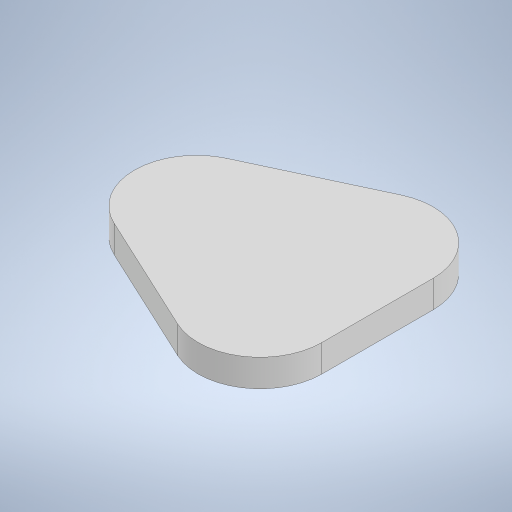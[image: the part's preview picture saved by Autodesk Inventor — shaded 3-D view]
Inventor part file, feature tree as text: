
AUTODESK INVENTOR PART (.ipt)
format: ipt  version: 2024.3 (Build 283343000, 343)  size: 261,120 bytes
history: native  units: in
note: dims shown in document units (in); Inventor stores cm internally (conversion verified against a paired STEP export)
features: extrude x3, sketch x3, projected_geometry x2
ambient origin geometry x8: Origin, YZ Plane, XZ Plane, XY Plane, X Axis, Y Axis, Z Axis, Center Point
bodies: Solid1 (feature_tree)
feature tree (8):
  extrude  "Extrusion1"  Depth=0.8583in
  extrude  "Extrusion2"  Depth=0.0394in
  extrude  "Extrusion3"  Depth=0.1575in
  sketch  "Sketch1"  dims[d0=0.3436in d1=0.8583in d2=1.2874in d3=0.8583in d4=0.8583in]
  sketch  "Sketch2"  dims[d5=0.0394in d6=0.0in d7=0.8926in]
  projected_geometry  "Projected Loop1"
  sketch  "Sketch3"  dims[d8=0.8926in d9=0.8926in d10=0.0394in d11=0.0in d12=0.8583in d13=0.8583in d14=0.8583in d15=0.1575in d16=0.0in d17=0.0197in d18=0.0344in d19=0.0197in d20=0.0344in]
  projected_geometry  "Projected Loop2"
